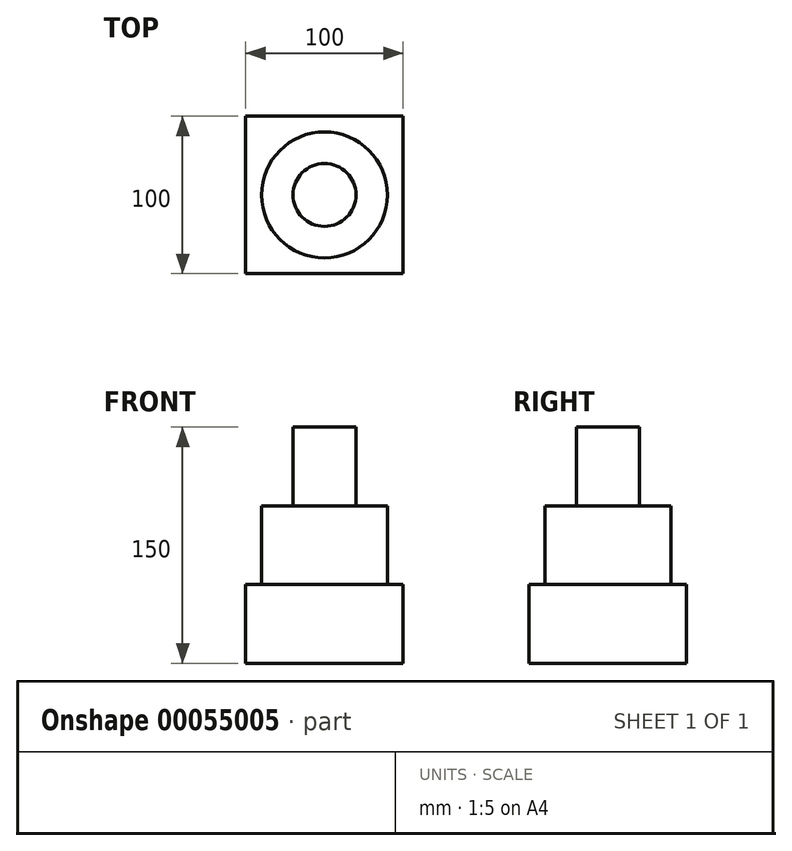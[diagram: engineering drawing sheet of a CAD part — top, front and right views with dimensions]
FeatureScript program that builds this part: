
annotation { "Feature Type Name" : "Feature", "Feature Type Description" : "" }
export const myFeature = defineFeature(function(context is Context, id is Id, definition is map)
    precondition{}
    {
        {
            var Q0;
            Q0=qCreatedBy(makeId("Top.planeOp"),FACE);
            var sketch = newSketch(context, id + "F0", { "sketchPlane" : qUnion([Q0])});
            skLineSegment(sketch, "E0.bottom", {"start": v(0, 0) * mm, "end": v(100, 0) * mm});
            skLineSegment(sketch, "E0.top", {"start": v(0, 100) * mm, "end": v(100, 100) * mm});
            skLineSegment(sketch, "E0.left", {"start": v(0, 0) * mm, "end": v(0, 100) * mm});
            skLineSegment(sketch, "E0.right", {"start": v(100, 0) * mm, "end": v(100, 100) * mm});
            skSolve(sketch);
        }
        {
            var Q0;
            Q0 = qSketchRegion(id + "F0", true);
            extrude(context, id + "F1", {"entities" : qUnion([Q0]), "depth" : 50 * mm});
        }
        {
            var Q0;
            Q0=makeQuery(id+"F1.opExtrude","CAP_FACE",FACE,{"disambiguationData":[OSD([sQuery(id+"F0.wireOp",EDGE,"E0.bottom"),sQuery(id+"F0.wireOp",EDGE,"E0.top"),sQuery(id+"F0.wireOp",EDGE,"E0.left"),sQuery(id+"F0.wireOp",EDGE,"E0.right")])],"isStart":false});
            var sketch = newSketch(context, id + "F2", { "sketchPlane" : qUnion([Q0])});
            skLineSegment(sketch, "E1", {"start": v(50, 100) * mm, "end": v(50, 0) * mm, "construction": true});
            skCircle(sketch, "E2", {"center": v(50, 50) * mm, "radius": 40 * mm});
            skSolve(sketch);
        }
        {
            var Q0;
            Q0=makeQuery(id+"F2.imprint","IMPRINT",FACE,{"disambiguationData":[TD([[makeQuery(id+"F2.imprint","IMPRINT",EDGE,{"derivedFrom":sQuery(id+"F2.wireOp",EDGE,"E2")}),1.0]])]});
            extrude(context, id + "F3", {"entities" : qUnion([Q0]), "operationType" : NewBodyOperationType.ADD, "depth" : 50 * mm});
        }
        {
            var Q0;
            Q0=makeQuery(id+"F3.opExtrude","CAP_FACE",FACE,{"disambiguationData":[OSD([sQuery(id+"F2.wireOp",EDGE,"E2")])],"isStart":false});
            var sketch = newSketch(context, id + "F4", { "sketchPlane" : qUnion([Q0])});
            skCircle(sketch, "E3", {"center": v(50, 50) * mm, "radius": 20 * mm});
            skSolve(sketch);
        }
        {
            var Q0;
            Q0=makeQuery(id+"F4.imprint","IMPRINT",FACE,{"disambiguationData":[TD([[makeQuery(id+"F4.imprint","IMPRINT",EDGE,{"derivedFrom":sQuery(id+"F4.wireOp",EDGE,"E3")}),1.0]])]});
            extrude(context, id + "F5", {"entities" : qUnion([Q0]), "operationType" : NewBodyOperationType.ADD, "depth" : 50 * mm});
        }
    });
